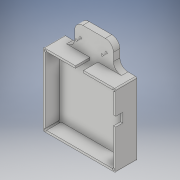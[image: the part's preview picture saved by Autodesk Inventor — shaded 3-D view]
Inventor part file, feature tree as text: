
AUTODESK INVENTOR PART (.ipt)
format: ipt  version: 2019 (Build 230136000, 136)  size: 209,920 bytes
history: native  units: mm
features: extrude x8, sketch x6, projected_geometry x4, fillet x2
ambient origin geometry x8: Origin, YZ Plane, XZ Plane, XY Plane, X Axis, Y Axis, Z Axis, Center Point
bodies: Solid1 (feature_tree)
feature tree (20):
  sketch  "Sketch1"  dims[d0=84.5mm d1=84.5mm]
  extrude  "Extrusion1"  Depth=84.5mm
  extrude  "Extrusion2"  Depth=90.0mm
  extrude  "Extrusion3"  Depth=8.0mm TaperAngle=0.0deg
  extrude  "Extrusion4"  Depth=3.0mm
  extrude  "Extrusion5"  Depth=3.0mm
  sketch  "Sketch5"  dims[d10=3.0mm d11=3.0mm]
  extrude  "Extrusion6"  Depth=10.0mm
  extrude  "Extrusion7"  Depth=11.5mm
  fillet  "Fillet1"  Radius=25.0mm
  fillet  "Fillet2"  Radius=9.5mm
  extrude  "Extrusion8"  Depth=10.0mm TaperAngle=0.0deg
  sketch  "Sketch2"  dims[d2=90.0mm d3=90.0mm]
  projected_geometry  "Projected Loop1"
  sketch  "Sketch3"  dims[d4=18.0mm d5=0.0mm d6=8.0mm d7=0.0mm]
  projected_geometry  "Projected Loop2"
  sketch  "Sketch4"  dims[d8=3.0mm d9=3.0mm]
  projected_geometry  "Projected Loop3"
  projected_geometry  "Projected Loop4"
  sketch  "Sketch6"  dims[d12=10.0mm d13=0.0mm d14=10.0mm d15=11.5mm d16=25.0mm d17=9.5mm d18=10.0mm d19=0.0mm d22=10.0mm d23=10.0mm d24=0.0mm d25=48.0mm d26=30.0mm d27=2.6mm d28=2.6mm d29=32.0mm d30=10.0mm d31=0.0mm d32=13.0mm d33=0.0mm d34=10.0mm d35=1.5mm d37=12.2mm d38=12.2mm d39=12.2mm d40=12.2mm d41=40.0mm d42=1.6mm d43=0.0mm]
